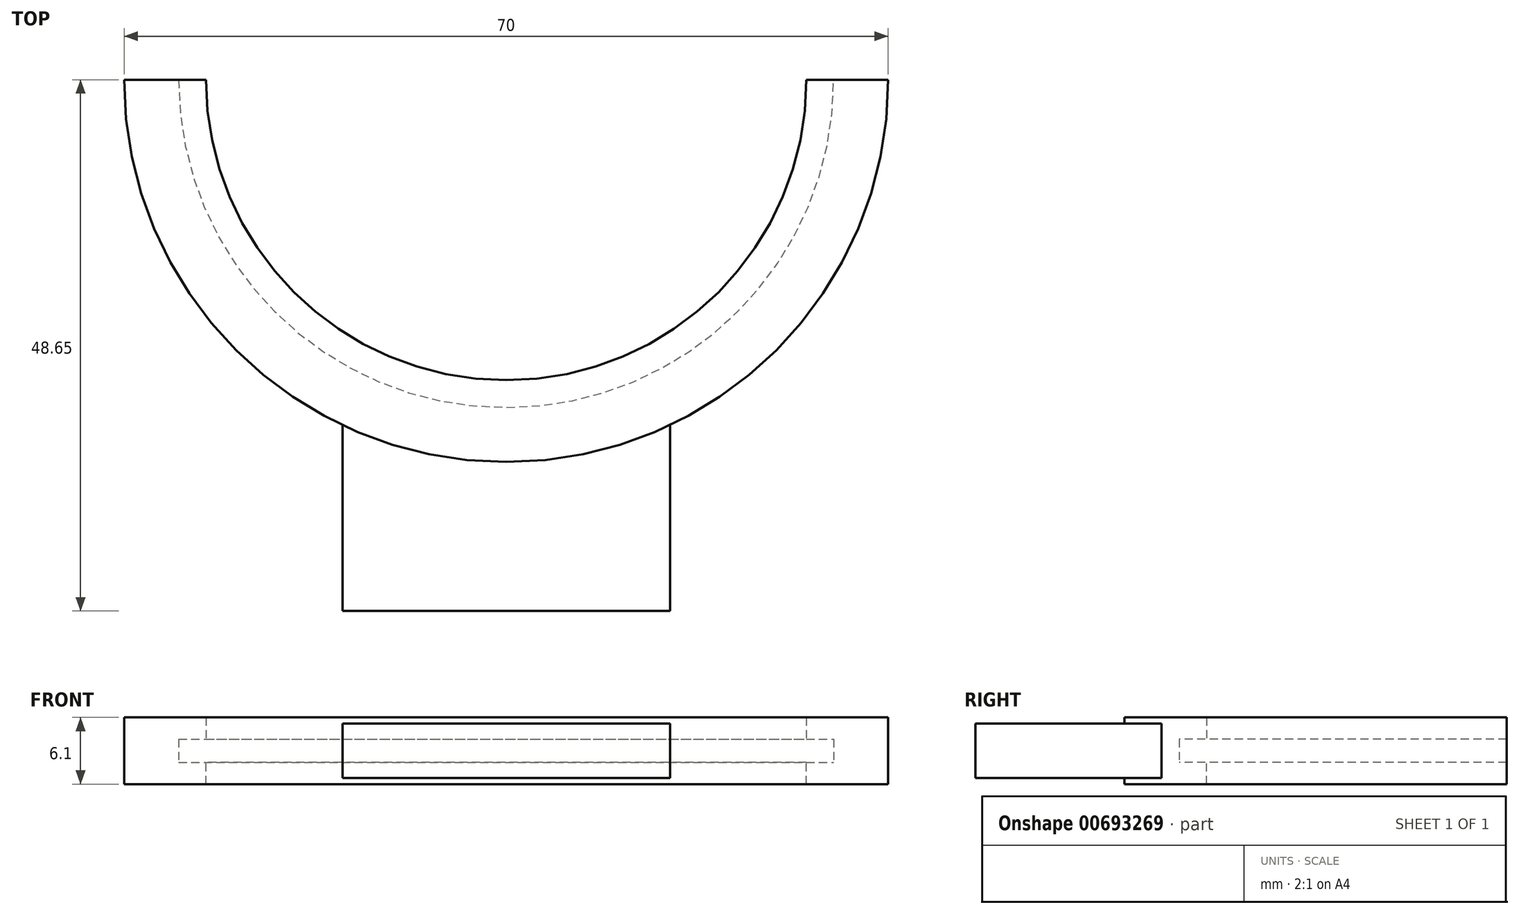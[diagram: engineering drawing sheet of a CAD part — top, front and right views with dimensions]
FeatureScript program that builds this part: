
annotation { "Feature Type Name" : "Feature", "Feature Type Description" : "" }
export const myFeature = defineFeature(function(context is Context, id is Id, definition is map)
    precondition{}
    {
        {
            var Q0;
            Q0=qCreatedBy(makeId("Top.planeOp"),FACE);
            var sketch = newSketch(context, id + "F0", { "sketchPlane" : qUnion([Q0])});
            skCircle(sketch, "E0", {"center": v(0, 0) * mm, "radius": 30 * mm});
            skCircle(sketch, "E1", {"center": v(0, 0) * mm, "radius": 35 * mm});
            skLineSegment(sketch, "E2.bottom", {"start": v(-35, 35) * mm, "end": v(35, 35) * mm, "construction": true});
            skLineSegment(sketch, "E2.top", {"start": v(-35, -35) * mm, "end": v(35, -35) * mm, "construction": true});
            skLineSegment(sketch, "E2.left", {"start": v(-35, 35) * mm, "end": v(-35, -35) * mm, "construction": true});
            skLineSegment(sketch, "E2.right", {"start": v(35, 35) * mm, "end": v(35, -35) * mm, "construction": true});
            skLineSegment(sketch, "E3", {"start": v(-35, 0) * mm, "end": v(35, 0) * mm});
            skSolve(sketch);
        }
        {
            var Q0;
            {var subQ0=sQuery(id+"F0.wireOp",EDGE,"E3");var subQ1=sQuery(id+"F0.wireOp",EDGE,"E0");var subQ2=makeQuery(id+"F0.imprint","INTERSECT",VERTEX,{"disambiguationData":[OD(0.0)],"derivedFrom":[subQ1,subQ0]});Q0=makeQuery(id+"F0.imprint","IMPRINT",FACE,{"disambiguationData":[TD([[makeQuery(id+"F0.imprint","IMPRINT",EDGE,{"disambiguationData":[TD([[subQ2,-1.0]])],"derivedFrom":subQ1}),-1.0]])]});}
            extrude(context, id + "F1", {"entities" : qUnion([Q0]), "endBound" : BoundingType.SYMMETRIC, "depth" : 2.1 * mm, "offsetDistance" : 25 * mm});
        }
        {
            var Q0;
            Q0=makeQuery(id+"F1.opExtrude","CAP_FACE",FACE,{"disambiguationData":[OSD([sQuery(id+"F0.wireOp",EDGE,"E0"),sQuery(id+"F0.wireOp",EDGE,"E1"),sQuery(id+"F0.wireOp",EDGE,"E3")])],"isStart":false});
            var sketch = newSketch(context, id + "F2", { "sketchPlane" : qUnion([Q0])});
            skCircle(sketch, "E4", {"center": v(0, 0) * mm, "radius": 35 * mm});
            skCircle(sketch, "E5", {"center": v(0, 0) * mm, "radius": 27.5 * mm});
            skLineSegment(sketch, "E6", {"start": v(35, 0) * mm, "end": v(-35, 0) * mm});
            skSolve(sketch);
        }
        {
            var Q0;
            {var subQ4=makeQuery(id+"F1.opExtrude","CAP_EDGE",EDGE,{"disambiguationData":[OSD([sQuery(id+"F0.wireOp",EDGE,"E0")])],"isStart":false});Q0=makeQuery(id+"F2.imprint","IMPRINT",FACE,{"disambiguationData":[TD([[makeQuery(id+"F2.imprint","IMPRINT",EDGE,{"derivedFrom":subQ4}),-1.0]])]});}
            var Q1;
            {var subQ4=makeQuery(id+"F1.opExtrude","CAP_EDGE",EDGE,{"disambiguationData":[OSD([sQuery(id+"F0.wireOp",EDGE,"E0")])],"isStart":false});Q1=makeQuery(id+"F2.imprint","IMPRINT",FACE,{"disambiguationData":[TD([[makeQuery(id+"F2.imprint","IMPRINT",EDGE,{"derivedFrom":subQ4}),1.0]])]});}
            extrude(context, id + "F3", {"entities" : qUnion([Q0, Q1]), "operationType" : NewBodyOperationType.ADD, "depth" : 2 * mm, "offsetDistance" : 25 * mm});
        }
        {
            var Q0;
            Q0=makeQuery(id+"F1.opExtrude","CAP_FACE",FACE,{"disambiguationData":[OSD([sQuery(id+"F0.wireOp",EDGE,"E0"),sQuery(id+"F0.wireOp",EDGE,"E1"),sQuery(id+"F0.wireOp",EDGE,"E3")])],"isStart":true});
            var sketch = newSketch(context, id + "F4", { "sketchPlane" : qUnion([Q0])});
            skCircle(sketch, "E7", {"center": v(0, 0) * mm, "radius": 35 * mm});
            skCircle(sketch, "E8", {"center": v(0, 0) * mm, "radius": 27.5 * mm});
            skLineSegment(sketch, "E9", {"start": v(35, 0) * mm, "end": v(-35, 0) * mm});
            skSolve(sketch);
        }
        {
            var Q0;
            {var subQ0=sQuery(id+"F4.wireOp",EDGE,"E7");Q0=makeQuery(id+"F4.imprint","IMPRINT",FACE,{"disambiguationData":[TD([[makeQuery(id+"F4.imprint","IMPRINT",EDGE,{"disambiguationData":[OD(1.0)],"derivedFrom":subQ0}),-1.0]])]});}
            var Q1;
            {var subQ4=makeQuery(id+"F1.opExtrude","CAP_EDGE",EDGE,{"disambiguationData":[OSD([sQuery(id+"F0.wireOp",EDGE,"E0")])],"isStart":true});Q1=makeQuery(id+"F4.imprint","IMPRINT",FACE,{"disambiguationData":[TD([[makeQuery(id+"F4.imprint","IMPRINT",EDGE,{"derivedFrom":subQ4}),-1.0]])]});}
            extrude(context, id + "F5", {"entities" : qUnion([Q0, Q1]), "operationType" : NewBodyOperationType.ADD, "depth" : 2 * mm, "offsetDistance" : 25 * mm});
        }
        {
            var Q0;
            Q0=qCreatedBy(makeId("Top.planeOp"),FACE);
            var sketch = newSketch(context, id + "F6", { "sketchPlane" : qUnion([Q0])});
            skLineSegment(sketch, "E10", {"start": v(0, -33.65) * mm, "end": v(0, -48.65) * mm});
            skLineSegment(sketch, "E11", {"start": v(0, -48.65) * mm, "end": v(15, -48.65) * mm});
            skLineSegment(sketch, "E12", {"start": v(15, -48.65) * mm, "end": v(15, -30.65) * mm});
            skArc(sketch, "E13", {"start": v(0, -33.65) * mm, "mid": v(7.62, -32.77) * mm, "end": v(15, -30.65) * mm});
            skArc(sketch, "E14.MirrorCS", {"start": v(0, -33.65) * mm, "mid": v(-7.62, -32.77) * mm, "end": v(-15, -30.65) * mm});
            skLineSegment(sketch, "E15.MirrorCS", {"start": v(-15, -48.65) * mm, "end": v(-15, -30.65) * mm});
            skLineSegment(sketch, "E16.MirrorCS", {"start": v(0, -48.65) * mm, "end": v(-15, -48.65) * mm});
            skSolve(sketch);
        }
        {
            var Q0;
            Q0=makeQuery(id+"F6.imprint","IMPRINT",FACE,{"disambiguationData":[TD([[makeQuery(id+"F6.imprint","IMPRINT",EDGE,{"derivedFrom":sQuery(id+"F6.wireOp",EDGE,"E10")}),-1.0]])]});
            var Q1;
            Q1=makeQuery(id+"F6.imprint","IMPRINT",FACE,{"disambiguationData":[TD([[makeQuery(id+"F6.imprint","IMPRINT",EDGE,{"derivedFrom":sQuery(id+"F6.wireOp",EDGE,"E10")}),1.0]])]});
            extrude(context, id + "F7", {"entities" : qUnion([Q0, Q1]), "operationType" : NewBodyOperationType.ADD, "endBound" : BoundingType.SYMMETRIC, "depth" : 5 * mm, "offsetDistance" : 25 * mm});
        }
    });
